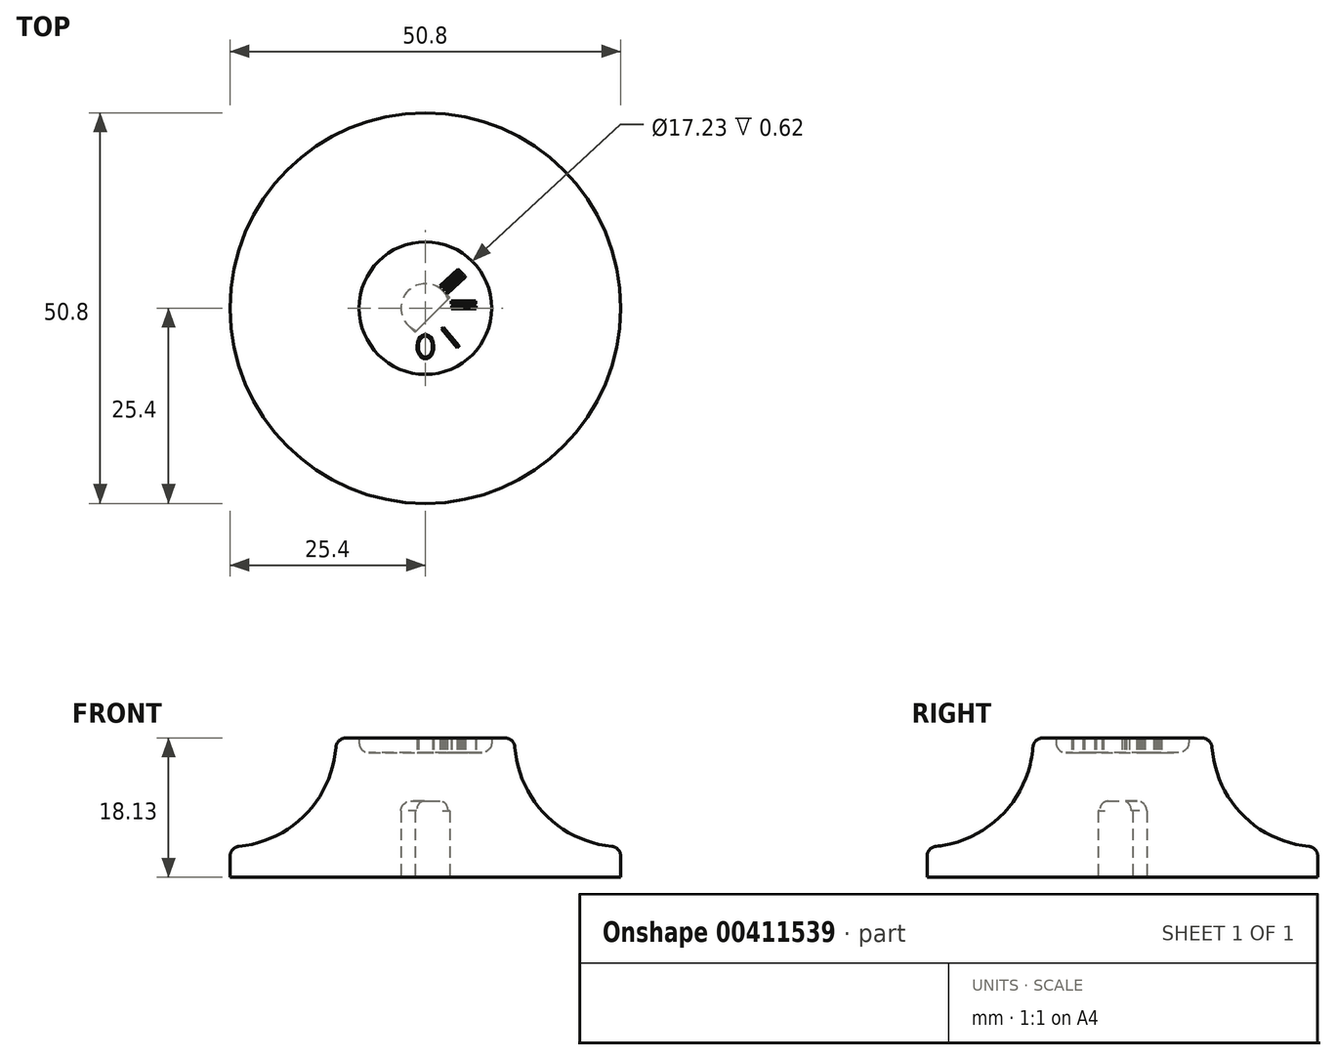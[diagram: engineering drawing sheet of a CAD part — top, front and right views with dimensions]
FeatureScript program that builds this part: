
annotation { "Feature Type Name" : "Feature", "Feature Type Description" : "" }
export const myFeature = defineFeature(function(context is Context, id is Id, definition is map)
    precondition{}
    {
        {
            var Q0;
            Q0=qCreatedBy(makeId("Front.planeOp"),FACE);
            var sketch = newSketch(context, id + "F0", { "sketchPlane" : qUnion([Q0])});
            skLineSegment(sketch, "E0", {"start": v(8.62, 0) * mm, "end": v(10.38, 0) * mm});
            skLineSegment(sketch, "E1", {"start": v(25.4, -18.1) * mm, "end": v(25.4, -15.34) * mm});
            skLineSegment(sketch, "E2", {"start": v(0, -8.2) * mm, "end": v(0, 0) * mm});
            skLineSegment(sketch, "E3", {"start": v(3.17, -18.1) * mm, "end": v(3.17, -9.47) * mm});
            skLineSegment(sketch, "E4", {"start": v(1.9, -8.2) * mm, "end": v(0, -8.2) * mm});
            skArc(sketch, "E5", {"start": v(11.64, -1.18) * mm, "mid": v(15.59, -9.93) * mm, "end": v(24.25, -14.07) * mm});
            skLineSegment(sketch, "E6.top", {"start": v(7.35, -1.89) * mm, "end": v(0, -1.89) * mm});
            skLineSegment(sketch, "E6.left", {"start": v(8.62, 0) * mm, "end": v(8.62, -0.62) * mm});
            skPoint(sketch, "E7.visualSharp", {"position": v(8.62, -1.89) * mm});
            skArc(sketch, "E7.filletArc", {"start": v(7.35, -1.89) * mm, "mid": v(8.24, -1.52) * mm, "end": v(8.62, -0.62) * mm});
            skPoint(sketch, "E8.visualSharp", {"position": v(3.17, -8.2) * mm});
            skArc(sketch, "E8.filletArc", {"start": v(3.17, -9.47) * mm, "mid": v(2.8, -8.57) * mm, "end": v(1.9, -8.2) * mm});
            skArc(sketch, "E9.filletArc", {"start": v(11.64, -1.18) * mm, "mid": v(11.24, -0.34) * mm, "end": v(10.38, 0) * mm});
            skArc(sketch, "E10.filletArc", {"start": v(25.4, -15.34) * mm, "mid": v(25.07, -14.48) * mm, "end": v(24.25, -14.07) * mm});
            skLineSegment(sketch, "E11", {"start": v(3.18, -18.1) * mm, "end": v(25.4, -18.1) * mm});
            skSolve(sketch);
        }
        {
            var Q0;
            Q0=makeQuery(id+"F0.imprint","IMPRINT",FACE,{"disambiguationData":[TD([[makeQuery(id+"F0.imprint","IMPRINT",EDGE,{"derivedFrom":sQuery(id+"F0.wireOp",EDGE,"E0")}),-1.0]])]});
            var Q1;
            Q1=sQuery(id+"F0.wireOp",EDGE,"E2");
            revolve(context, id + "F1", {"entities" : qUnion([Q0]), "axis" : qUnion([Q1]), "revolveType" : RevolveType.FULL});
        }
        {
            var Q0;
            Q0=makeQuery(id+"F1.opRevolve","SWEPT_FACE",FACE,{"disambiguationData":[OSD([sQuery(id+"F0.wireOp",EDGE,"E11")])]});
            var sketch = newSketch(context, id + "F2", { "sketchPlane" : qUnion([Q0])});
            skLineSegment(sketch, "E12", {"start": v(1.27, 2.9) * mm, "end": v(1.27, -2.9) * mm});
            skArc(sketch, "E13", {"start": v(1.27, -2.9) * mm, "mid": v(3.18, 0) * mm, "end": v(1.27, 2.9) * mm});
            skLineSegment(sketch, "E14", {"start": v(1.27, 2.9) * mm, "end": v(0, 3.18) * mm});
            skLineSegment(sketch, "E15", {"start": v(1.27, 2.9) * mm, "end": v(1.27, 3.18) * mm});
            skLineSegment(sketch, "E16", {"start": v(1.27, 3.18) * mm, "end": v(0, 3.18) * mm});
            skLineSegment(sketch, "E17", {"start": v(0, -3.18) * mm, "end": v(1.27, -2.9) * mm});
            skLineSegment(sketch, "E18", {"start": v(0, -3.18) * mm, "end": v(1.27, -3.18) * mm});
            skLineSegment(sketch, "E19", {"start": v(1.27, -3.18) * mm, "end": v(1.27, -2.9) * mm});
            skSolve(sketch);
        }
        {
            var Q0;
            {var subQ0=sQuery(id+"F2.wireOp",EDGE,"E15");Q0=makeQuery(id+"F2.imprint","IMPRINT",FACE,{"disambiguationData":[TD([[makeQuery(id+"F2.imprint","IMPRINT",EDGE,{"derivedFrom":subQ0}),1.0]])]});}
            extrude(context, id + "F3", {"entities" : qUnion([Q0]), "operationType" : NewBodyOperationType.REMOVE, "oppositeDirection" : true, "depth" : 8.64 * mm});
        }
        {
            var Q0;
            {var subQ0=sQuery(id+"F2.wireOp",EDGE,"E18");Q0=makeQuery(id+"F2.imprint","IMPRINT",FACE,{"disambiguationData":[TD([[makeQuery(id+"F2.imprint","IMPRINT",EDGE,{"derivedFrom":subQ0}),1.0]])]});}
            extrude(context, id + "F4", {"entities" : qUnion([Q0]), "operationType" : NewBodyOperationType.REMOVE, "oppositeDirection" : true, "depth" : 8.64 * mm});
        }
        {
            var Q0;
            Q0=makeQuery(id+"F2.imprint","IMPRINT",FACE,{"disambiguationData":[TD([[makeQuery(id+"F2.imprint","IMPRINT",EDGE,{"derivedFrom":sQuery(id+"F2.wireOp",EDGE,"E12")}),1.0]])]});
            extrude(context, id + "F5", {"entities" : qUnion([Q0]), "operationType" : NewBodyOperationType.ADD, "oppositeDirection" : true, "depth" : 9.9 * mm});
        }
        {
            var Q0;
            Q0=qCreatedBy(makeId("Right.planeOp"),FACE);
            var sketch = newSketch(context, id + "F6", { "sketchPlane" : qUnion([Q0])});
            skLineSegment(sketch, "E20", {"start": v(0, 0) * mm, "end": v(0, 22.38) * mm});
            skSolve(sketch);
        }
        {
            var Q0;
            Q0=makeQuery(id+"F1.opRevolve","SWEPT_BODY",BODY,{"disambiguationData":[OSD([sQuery(id+"F0.wireOp",EDGE,"E0"),sQuery(id+"F0.wireOp",EDGE,"E1"),sQuery(id+"F0.wireOp",EDGE,"E2"),sQuery(id+"F0.wireOp",EDGE,"E3"),sQuery(id+"F0.wireOp",EDGE,"E4"),sQuery(id+"F0.wireOp",EDGE,"E5"),sQuery(id+"F0.wireOp",EDGE,"E6.top"),sQuery(id+"F0.wireOp",EDGE,"E6.left"),sQuery(id+"F0.wireOp",EDGE,"E7.filletArc"),sQuery(id+"F0.wireOp",EDGE,"E8.filletArc"),sQuery(id+"F0.wireOp",EDGE,"E9.filletArc"),sQuery(id+"F0.wireOp",EDGE,"E10.filletArc"),sQuery(id+"F0.wireOp",EDGE,"E11")])]});
            var Q1;
            Q1=sQuery(id+"F6.wireOp",EDGE,"E20");
            transform(context, id + "F7", {"entities" : qUnion([Q0]), "transformType" : TransformType.ROTATION, "transformAxis" : qUnion([Q1]), "angle" : 315 * degree, "makeCopy" : false});
        }
        {
            var Q0;
            Q0=makeQuery(id+"F1.opRevolve","SWEPT_FACE",FACE,{"disambiguationData":[OSD([sQuery(id+"F0.wireOp",EDGE,"E6.top")])]});
            var sketch = newSketch(context, id + "F8", { "sketchPlane" : qUnion([Q0])});
            skEllipse(sketch, "E21", {"center": v(0, -5) * mm, "majorRadius": 1.38 * mm, "minorRadius": 0.92 * mm, "majorAxis": v(0, -1)});
            skEllipse(sketch, "E22", {"center": v(0, -5) * mm, "majorRadius": 1.59 * mm, "minorRadius": 1.09 * mm, "majorAxis": v(0, -1)});
            skArc(sketch, "E23.MirrorCS", {"start": v(6.6, 0.3) * mm, "mid": v(6.61, 0.1) * mm, "end": v(6.62, -0.08) * mm});
            skLineSegment(sketch, "E24.MirrorCS", {"start": v(4.83, 4.5) * mm, "end": v(4.64, 4.7) * mm});
            skLineSegment(sketch, "E25.MirrorCS", {"start": v(4.64, 4.7) * mm, "end": v(4.88, 4.45) * mm});
            skArc(sketch, "E26.MirrorCS", {"start": v(5.01, 4.3) * mm, "mid": v(5.1, 4.18) * mm, "end": v(5.2, 4.06) * mm});
            skLineSegment(sketch, "E27.MirrorCS", {"start": v(4.14, -5.14) * mm, "end": v(4.38, -4.94) * mm});
            skLineSegment(sketch, "E28.MirrorCS", {"start": v(4.22, 5.08) * mm, "end": v(4.48, 4.85) * mm});
            skArc(sketch, "E29.MirrorCS", {"start": v(4.64, 4.7) * mm, "mid": v(4.76, 4.57) * mm, "end": v(4.88, 4.45) * mm});
            skLineSegment(sketch, "E30.MirrorCS", {"start": v(5.2, 4.06) * mm, "end": v(5.01, 4.3) * mm});
            skArc(sketch, "E31.MirrorCS", {"start": v(4.38, -4.94) * mm, "mid": v(4.26, -5.04) * mm, "end": v(4.14, -5.14) * mm});
            skLineSegment(sketch, "E32.MirrorCS", {"start": v(2.67, 2.12) * mm, "end": v(2.85, 1.87) * mm});
            skArc(sketch, "E33.MirrorCS", {"start": v(4.22, 5.08) * mm, "mid": v(4.35, 4.97) * mm, "end": v(4.48, 4.85) * mm});
            skArc(sketch, "E34.MirrorCS", {"start": v(2.3, 2.52) * mm, "mid": v(2.43, 2.4) * mm, "end": v(2.55, 2.27) * mm});
            skLineSegment(sketch, "E35.MirrorCS", {"start": v(2.13, 2.67) * mm, "end": v(1.9, 2.91) * mm});
            skArc(sketch, "E36.MirrorCS", {"start": v(2.67, 2.12) * mm, "mid": v(2.77, 2) * mm, "end": v(2.85, 1.87) * mm});
            skLineSegment(sketch, "E37.MirrorCS", {"start": v(2.3, 2.52) * mm, "end": v(2.55, 2.27) * mm});
            skLineSegment(sketch, "E38.MirrorCS", {"start": v(6.55, 0.55) * mm, "end": v(6.55, 0.9) * mm});
            skLineSegment(sketch, "E39.MirrorCS", {"start": v(2.34, -2.48) * mm, "end": v(2.1, -2.68) * mm});
            skArc(sketch, "E40.MirrorCS", {"start": v(2.34, -2.48) * mm, "mid": v(2.26, -2.56) * mm, "end": v(2.18, -2.63) * mm});
            skLineSegment(sketch, "E41.MirrorCS", {"start": v(3.37, 0.55) * mm, "end": v(3.37, 0.9) * mm});
            skLineSegment(sketch, "E42.MirrorCS", {"start": v(4.48, 4.85) * mm, "end": v(2.13, 2.67) * mm});
            skLineSegment(sketch, "E43.MirrorCS", {"start": v(4.88, 4.45) * mm, "end": v(2.55, 2.27) * mm});
            skLineSegment(sketch, "E44.MirrorCS", {"start": v(5.01, 4.3) * mm, "end": v(2.67, 2.12) * mm});
            skLineSegment(sketch, "E45.MirrorCS", {"start": v(2.55, 2.27) * mm, "end": v(2.55, 2.27) * mm});
            skPoint(sketch, "E46.MirrorP", {"position": v(3.3, 0) * mm});
            skLineSegment(sketch, "E47.MirrorCS", {"start": v(1.9, 2.91) * mm, "end": v(4.22, 5.08) * mm});
            skLineSegment(sketch, "E48.MirrorCS", {"start": v(3.37, -0.08) * mm, "end": v(6.62, -0.08) * mm});
            skLineSegment(sketch, "E49.MirrorCS", {"start": v(4.83, 4.5) * mm, "end": v(4.88, 4.45) * mm});
            skLineSegment(sketch, "E50.MirrorCS", {"start": v(4.64, 4.7) * mm, "end": v(2.3, 2.52) * mm});
            skLineSegment(sketch, "E51.MirrorCS", {"start": v(2.85, 1.87) * mm, "end": v(5.2, 4.06) * mm});
            skLineSegment(sketch, "E52.MirrorCS", {"start": v(3.37, 0.55) * mm, "end": v(6.55, 0.55) * mm});
            skLineSegment(sketch, "E53.MirrorCS", {"start": v(6.6, 0.3) * mm, "end": v(3.4, 0.3) * mm});
            skLineSegment(sketch, "E54.MirrorCS", {"start": v(4.38, -4.94) * mm, "end": v(2.34, -2.48) * mm});
            skLineSegment(sketch, "E55.MirrorCS", {"start": v(2.1, -2.68) * mm, "end": v(4.14, -5.14) * mm});
            skLineSegment(sketch, "E56.MirrorCS", {"start": v(3.37, 0.9) * mm, "end": v(6.55, 0.9) * mm});
            skLineSegment(sketch, "E57", {"start": v(3.37, -0.08) * mm, "end": v(3.4, 0.3) * mm});
            skSolve(sketch);
        }
        {
            var Q0;
            Q0 = qSketchRegion(id + "F8", true);
            extrude(context, id + "F9", {"entities" : qUnion([Q0]), "operationType" : NewBodyOperationType.ADD, "depth" : 1.9 * mm});
        }
    });
